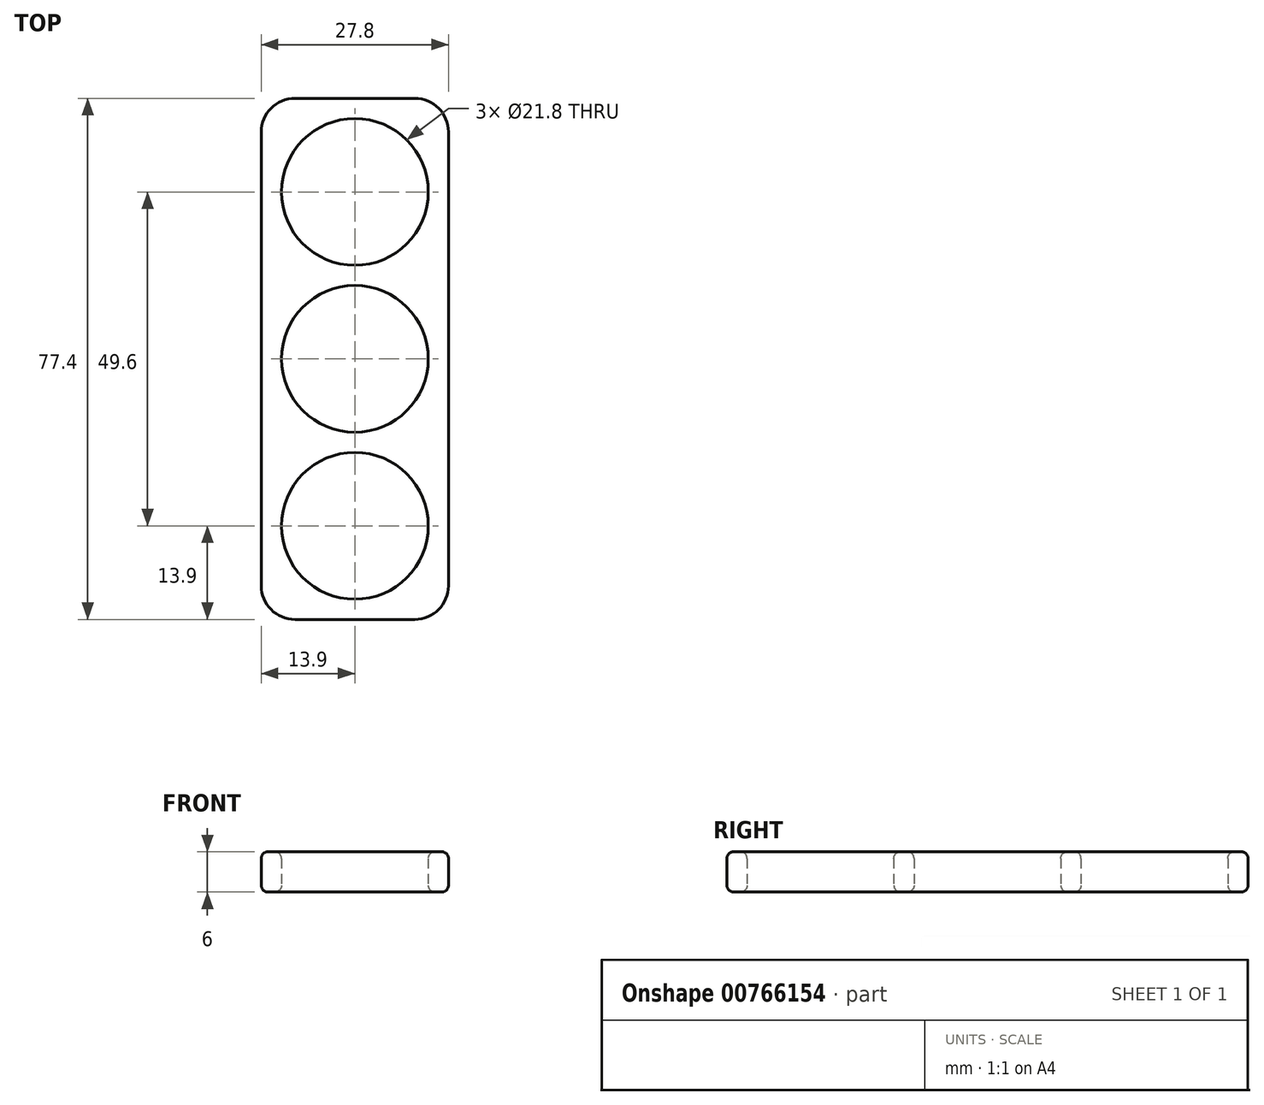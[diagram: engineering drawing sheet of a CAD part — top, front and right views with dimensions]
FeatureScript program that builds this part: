
annotation { "Feature Type Name" : "Feature", "Feature Type Description" : "" }
export const myFeature = defineFeature(function(context is Context, id is Id, definition is map)
    precondition{}
    {
        {
            assignVariable(context, id + "F0", {"name" : "bearingH", "anyValue" : 6});
        }
        {
            assignVariable(context, id + "F1", {"name" : "fillet", "anyValue" : 1});
        }
        {
            var Q0;
            Q0=qCreatedBy(makeId("Top.planeOp"),FACE);
            var sketch = newSketch(context, id + "F2", { "sketchPlane" : qUnion([Q0])});
            skCircle(sketch, "E0", {"center": v(0, 0) * mm, "radius": 10.9 * mm});
            skCircle(sketch, "E1", {"center": v(0, 24.8) * mm, "radius": 10.9 * mm});
            skCircle(sketch, "E2.MirrorC", {"center": v(0, -24.8) * mm, "radius": 10.9 * mm});
            skLineSegment(sketch, "E3.bottom", {"start": v(8.9, 38.7) * mm, "end": v(-8.9, 38.7) * mm});
            skLineSegment(sketch, "E3.top", {"start": v(8.9, -38.7) * mm, "end": v(-8.9, -38.7) * mm});
            skLineSegment(sketch, "E3.left", {"start": v(13.9, 33.7) * mm, "end": v(13.9, -33.7) * mm});
            skLineSegment(sketch, "E3.right", {"start": v(-13.9, 33.7) * mm, "end": v(-13.9, -33.7) * mm});
            skPoint(sketch, "E4.visualSharp", {"position": v(-13.9, 38.7) * mm});
            skArc(sketch, "E4.filletArc", {"start": v(-8.9, 38.7) * mm, "mid": v(-12.44, 37.24) * mm, "end": v(-13.9, 33.7) * mm});
            skPoint(sketch, "E5.visualSharp", {"position": v(13.9, 38.7) * mm});
            skArc(sketch, "E5.filletArc", {"start": v(13.9, 33.7) * mm, "mid": v(12.44, 37.24) * mm, "end": v(8.9, 38.7) * mm});
            skPoint(sketch, "E6.visualSharp", {"position": v(13.9, -38.7) * mm});
            skArc(sketch, "E6.filletArc", {"start": v(8.9, -38.7) * mm, "mid": v(12.44, -37.24) * mm, "end": v(13.9, -33.7) * mm});
            skPoint(sketch, "E7.visualSharp", {"position": v(-13.9, -38.7) * mm});
            skArc(sketch, "E7.filletArc", {"start": v(-13.9, -33.7) * mm, "mid": v(-12.44, -37.24) * mm, "end": v(-8.9, -38.7) * mm});
            skSolve(sketch);
        }
        {
            var Q0;
            Q0=makeQuery(id+"F2.imprint","IMPRINT",FACE,{"disambiguationData":[TD([[makeQuery(id+"F2.imprint","IMPRINT",EDGE,{"derivedFrom":sQuery(id+"F2.wireOp",EDGE,"E0")}),-1.0]])]});
            extrude(context, id + "F3", {"entities" : qUnion([Q0]), "depth" : (getVariable(context, 'bearingH')) * mm, "offsetDistance" : 25 * mm});
        }
        {
            var Q0;
            Q0=makeQuery(id+"F3.opExtrude","CAP_FACE",FACE,{"disambiguationData":[OSD([sQuery(id+"F2.wireOp",EDGE,"E0"),sQuery(id+"F2.wireOp",EDGE,"E1"),sQuery(id+"F2.wireOp",EDGE,"E2.MirrorC"),sQuery(id+"F2.wireOp",EDGE,"E3.bottom"),sQuery(id+"F2.wireOp",EDGE,"E3.top"),sQuery(id+"F2.wireOp",EDGE,"E3.left"),sQuery(id+"F2.wireOp",EDGE,"E3.right"),sQuery(id+"F2.wireOp",EDGE,"E4.filletArc"),sQuery(id+"F2.wireOp",EDGE,"E5.filletArc"),sQuery(id+"F2.wireOp",EDGE,"E6.filletArc"),sQuery(id+"F2.wireOp",EDGE,"E7.filletArc")])],"isStart":false});
            var Q1;
            Q1=makeQuery(id+"F3.opExtrude","CAP_FACE",FACE,{"disambiguationData":[OSD([sQuery(id+"F2.wireOp",EDGE,"E0"),sQuery(id+"F2.wireOp",EDGE,"E1"),sQuery(id+"F2.wireOp",EDGE,"E2.MirrorC"),sQuery(id+"F2.wireOp",EDGE,"E3.bottom"),sQuery(id+"F2.wireOp",EDGE,"E3.top"),sQuery(id+"F2.wireOp",EDGE,"E3.left"),sQuery(id+"F2.wireOp",EDGE,"E3.right"),sQuery(id+"F2.wireOp",EDGE,"E4.filletArc"),sQuery(id+"F2.wireOp",EDGE,"E5.filletArc"),sQuery(id+"F2.wireOp",EDGE,"E6.filletArc"),sQuery(id+"F2.wireOp",EDGE,"E7.filletArc")])],"isStart":true});
            fillet(context, id + "F4", {"entities" : qUnion([Q0, Q1]), "radius" : (getVariable(context, 'fillet')) * mm, "tangentPropagation" : true, "allowEdgeOverflow" : false});
        }
    });
